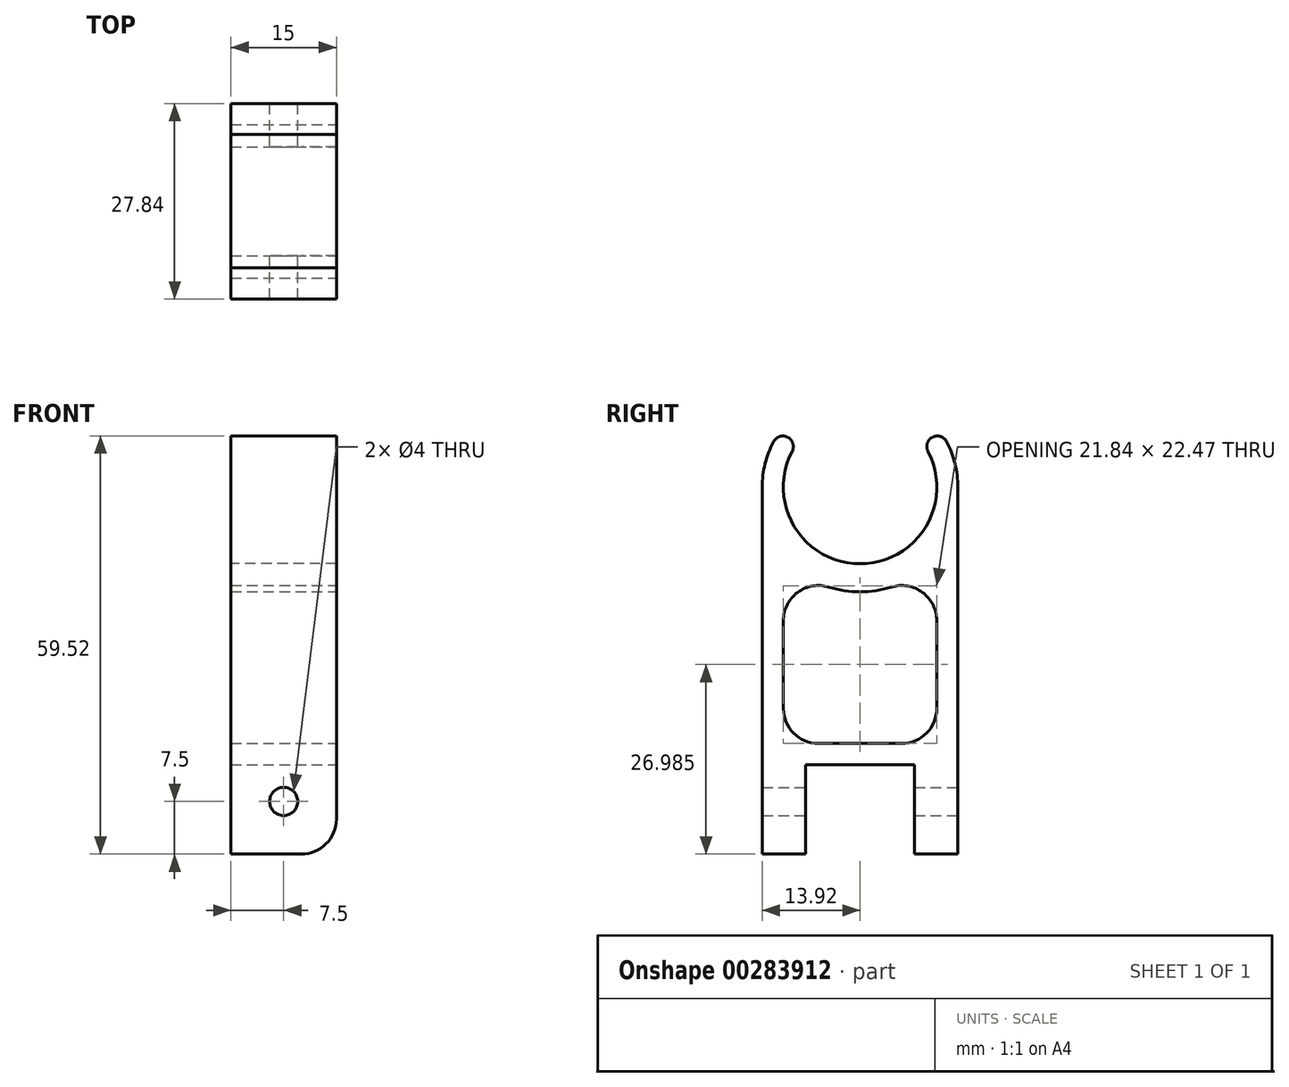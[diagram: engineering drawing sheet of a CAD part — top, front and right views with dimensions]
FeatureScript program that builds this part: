
annotation { "Feature Type Name" : "Feature", "Feature Type Description" : "" }
export const myFeature = defineFeature(function(context is Context, id is Id, definition is map)
    precondition{}
    {
        {
            var Q0;
            Q0=qCreatedBy(makeId("Right.planeOp"),FACE);
            var sketch = newSketch(context, id + "F0", { "sketchPlane" : qUnion([Q0])});
            skCircle(sketch, "E0", {"center": v(0, 0) * mm, "radius": 10.92 * mm, "construction": true});
            skLineSegment(sketch, "E1", {"start": v(0, 0) * mm, "end": v(0, -86) * mm, "construction": true});
            skPoint(sketch, "E2", {"position": v(0, -44.75) * mm});
            skPoint(sketch, "E3", {"position": v(0, -40) * mm});
            skArc(sketch, "E4", {"start": v(9.67, 5.07) * mm, "mid": v(0, -10.92) * mm, "end": v(-9.67, 5.07) * mm});
            skLineSegment(sketch, "E5", {"start": v(0, 0) * mm, "end": v(0, 10.92) * mm, "construction": true});
            skLineSegment(sketch, "E6", {"start": v(0, 7.27) * mm, "end": v(33.13, 7.27) * mm, "construction": true});
            skArc(sketch, "E7", {"start": v(-12.32, 6.47) * mm, "mid": v(0, -13.92) * mm, "end": v(12.32, 6.47) * mm});
            skArc(sketch, "E8", {"start": v(-9.67, 5.07) * mm, "mid": v(-10.3, 7.1) * mm, "end": v(-12.32, 6.47) * mm});
            skArc(sketch, "E9.MirrorCS", {"start": v(9.67, 5.07) * mm, "mid": v(10.3, 7.1) * mm, "end": v(12.32, 6.47) * mm});
            skSolve(sketch);
        }
        {
            var Q0;
            Q0 = qSketchRegion(id + "F0", true);
            extrude(context, id + "F1", {"entities" : qUnion([Q0]), "endBound" : BoundingType.SYMMETRIC, "depth" : 15 * mm});
        }
        {
            var Q0;
            Q0=makeQuery(id+"F1.opExtrude","CAP_FACE",FACE,{"disambiguationData":[OSD([sQuery(id+"F0.wireOp",EDGE,"E4"),sQuery(id+"F0.wireOp",EDGE,"E7"),sQuery(id+"F0.wireOp",EDGE,"E8"),sQuery(id+"F0.wireOp",EDGE,"E9.MirrorCS")])],"isStart":false});
            var sketch = newSketch(context, id + "F2", { "sketchPlane" : qUnion([Q0])});
            skLineSegment(sketch, "E10", {"start": v(0, 0) * mm, "end": v(0, -86) * mm, "construction": true});
            skPoint(sketch, "E11", {"position": v(0, -44.75) * mm});
            skPoint(sketch, "E12", {"position": v(0, -40) * mm});
            skArc(sketch, "E13.0", {"start": v(-12.32, 6.47) * mm, "mid": v(0, -13.92) * mm, "end": v(12.32, 6.47) * mm});
            skArc(sketch, "E13.1", {"start": v(-13.92, 0) * mm, "mid": v(0, -13.92) * mm, "end": v(13.92, 0) * mm});
            skLineSegment(sketch, "E14", {"start": v(-13.92, 0) * mm, "end": v(-13.92, -52.25) * mm});
            skLineSegment(sketch, "E15", {"start": v(-13.92, -52.25) * mm, "end": v(-7.75, -52.25) * mm});
            skLineSegment(sketch, "E16", {"start": v(-7.75, -52.25) * mm, "end": v(-7.75, -39.5) * mm});
            skLineSegment(sketch, "E17.MirrorCS", {"start": v(13.92, -52.25) * mm, "end": v(7.75, -52.25) * mm});
            skLineSegment(sketch, "E18.MirrorCS", {"start": v(7.75, -52.25) * mm, "end": v(7.75, -39.5) * mm});
            skLineSegment(sketch, "E19.MirrorCS", {"start": v(13.92, 0) * mm, "end": v(13.92, -52.25) * mm});
            skPoint(sketch, "E20.orphan", {"position": v(12.32, 6.47) * mm});
            skPoint(sketch, "E21.orphan", {"position": v(-12.32, 6.47) * mm});
            skLineSegment(sketch, "E22", {"start": v(-7.75, -39.5) * mm, "end": v(7.75, -39.5) * mm});
            skArc(sketch, "E23", {"start": v(-10.92, -10.17) * mm, "mid": v(0, -14.92) * mm, "end": v(10.92, -10.17) * mm});
            skLineSegment(sketch, "E24", {"start": v(-10.92, -10.17) * mm, "end": v(-10.92, -36.5) * mm});
            skLineSegment(sketch, "E25", {"start": v(-10.92, -36.5) * mm, "end": v(10.92, -36.5) * mm});
            skLineSegment(sketch, "E26.MirrorCS", {"start": v(10.92, -10.17) * mm, "end": v(10.92, -36.5) * mm});
            skSolve(sketch);
        }
        {
            var Q0;
            Q0 = qSketchRegion(id + "F2", true);
            var Q1;
            Q1=makeQuery(id+"F1.opExtrude","CAP_FACE",FACE,{"disambiguationData":[OSD([sQuery(id+"F0.wireOp",EDGE,"E4"),sQuery(id+"F0.wireOp",EDGE,"E7"),sQuery(id+"F0.wireOp",EDGE,"E8"),sQuery(id+"F0.wireOp",EDGE,"E9.MirrorCS")])],"isStart":true});
            extrude(context, id + "F3", {"entities" : qUnion([Q0]), "operationType" : NewBodyOperationType.ADD, "endBound" : BoundingType.UP_TO_SURFACE, "oppositeDirection" : true, "endBoundEntityFace" : qUnion([Q1]), "depth" : 25 * mm});
        }
        {
            var Q0;
            Q0=makeQuery(id+"F3.opExtrude","SWEPT_FACE",FACE,{"disambiguationData":[OSD([sQuery(id+"F2.wireOp",EDGE,"E19.MirrorCS")])]});
            var sketch = newSketch(context, id + "F4", { "sketchPlane" : qUnion([Q0])});
            skLineSegment(sketch, "E27.0", {"start": v(7.5, -39.5) * mm, "end": v(-7.5, -39.5) * mm, "construction": true});
            skLineSegment(sketch, "E28", {"start": v(0, -39.5) * mm, "end": v(0, -52.25) * mm, "construction": true});
            skCircle(sketch, "E29", {"center": v(0, -44.75) * mm, "radius": 2 * mm});
            skSolve(sketch);
        }
        {
            var Q0;
            Q0 = qSketchRegion(id + "F4", true);
            extrude(context, id + "F5", {"entities" : qUnion([Q0]), "operationType" : NewBodyOperationType.REMOVE, "endBound" : BoundingType.THROUGH_ALL, "oppositeDirection" : true, "depth" : 25 * mm});
        }
        {
            var Q0;
            Q0=makeQuery(id+"F3.opExtrude","CAP_EDGE",EDGE,{"disambiguationData":[OSD([sQuery(id+"F2.wireOp",EDGE,"E15")])],"isStart":true});
            var Q1;
            Q1=makeQuery(id+"F3.opExtrude","TWEAK_EDGE",EDGE,{"derivedFrom":[makeQuery(id+"F1.opExtrude","CAP_FACE",FACE,{"disambiguationData":[OSD([sQuery(id+"F0.wireOp",EDGE,"E4"),sQuery(id+"F0.wireOp",EDGE,"E7"),sQuery(id+"F0.wireOp",EDGE,"E8"),sQuery(id+"F0.wireOp",EDGE,"E9.MirrorCS")])],"isStart":true}),makeQuery(id+"F2.imprint","IMPRINT",EDGE,{"derivedFrom":sQuery(id+"F2.wireOp",EDGE,"E15")})]});
            var Q2;
            Q2=makeQuery(id+"F3.opExtrude","CAP_EDGE",EDGE,{"disambiguationData":[OSD([sQuery(id+"F2.wireOp",EDGE,"E17.MirrorCS")])],"isStart":true});
            var Q3;
            Q3=makeQuery(id+"F3.opExtrude","TWEAK_EDGE",EDGE,{"derivedFrom":[makeQuery(id+"F1.opExtrude","CAP_FACE",FACE,{"disambiguationData":[OSD([sQuery(id+"F0.wireOp",EDGE,"E4"),sQuery(id+"F0.wireOp",EDGE,"E7"),sQuery(id+"F0.wireOp",EDGE,"E8"),sQuery(id+"F0.wireOp",EDGE,"E9.MirrorCS")])],"isStart":true}),makeQuery(id+"F2.imprint","IMPRINT",EDGE,{"derivedFrom":sQuery(id+"F2.wireOp",EDGE,"E17.MirrorCS")})]});
            var Q4;
            Q4=makeQuery(id+"F3.opExtrude","SWEPT_EDGE",EDGE,{"disambiguationData":[OSD([sQuery(id+"F2.wireOp",EDGE,"E23"),sQuery(id+"F2.wireOp",EDGE,"E24")])]});
            var Q5;
            Q5=makeQuery(id+"F3.opExtrude","SWEPT_EDGE",EDGE,{"disambiguationData":[OSD([sQuery(id+"F2.wireOp",EDGE,"E23"),sQuery(id+"F2.wireOp",EDGE,"E26.MirrorCS")])]});
            var Q6;
            Q6=makeQuery(id+"F3.opExtrude","SWEPT_EDGE",EDGE,{"disambiguationData":[OSD([sQuery(id+"F2.wireOp",EDGE,"E24"),sQuery(id+"F2.wireOp",EDGE,"E25")])]});
            var Q7;
            Q7=makeQuery(id+"F3.opExtrude","SWEPT_EDGE",EDGE,{"disambiguationData":[OSD([sQuery(id+"F2.wireOp",EDGE,"E25"),sQuery(id+"F2.wireOp",EDGE,"E26.MirrorCS")])]});
            fillet(context, id + "F6", {"entities" : qUnion([Q0, Q1, Q2, Q3, Q4, Q5, Q6, Q7]), "radius" : 5 * mm, "tangentPropagation" : true, "allowEdgeOverflow" : false});
        }
    });
